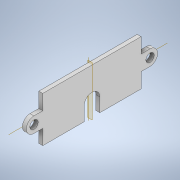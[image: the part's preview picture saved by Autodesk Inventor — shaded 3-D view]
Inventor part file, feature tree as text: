
AUTODESK INVENTOR PART (.ipt)
format: ipt  version: 2021 (Build 250183000, 183)  size: 135,168 bytes
history: native  units: mm
features: extrude x1, mirror x1, sketch x1
ambient origin geometry x8: Origin, YZ Plane, XZ Plane, XY Plane, X Axis, Y Axis, Z Axis, Center Point
bodies: Solid1 (feature_tree)
feature tree (3):
  extrude  "Extrusion1"  Depth=23.0mm
  mirror  "Mirror1"
  sketch  "Sketch1"  dims[d0=50.0mm d1=23.0mm d2=2.0mm d3=0.0mm d4=7.75mm d5=4.5mm d6=4.2mm d11=8.0mm d12=7.0mm]
